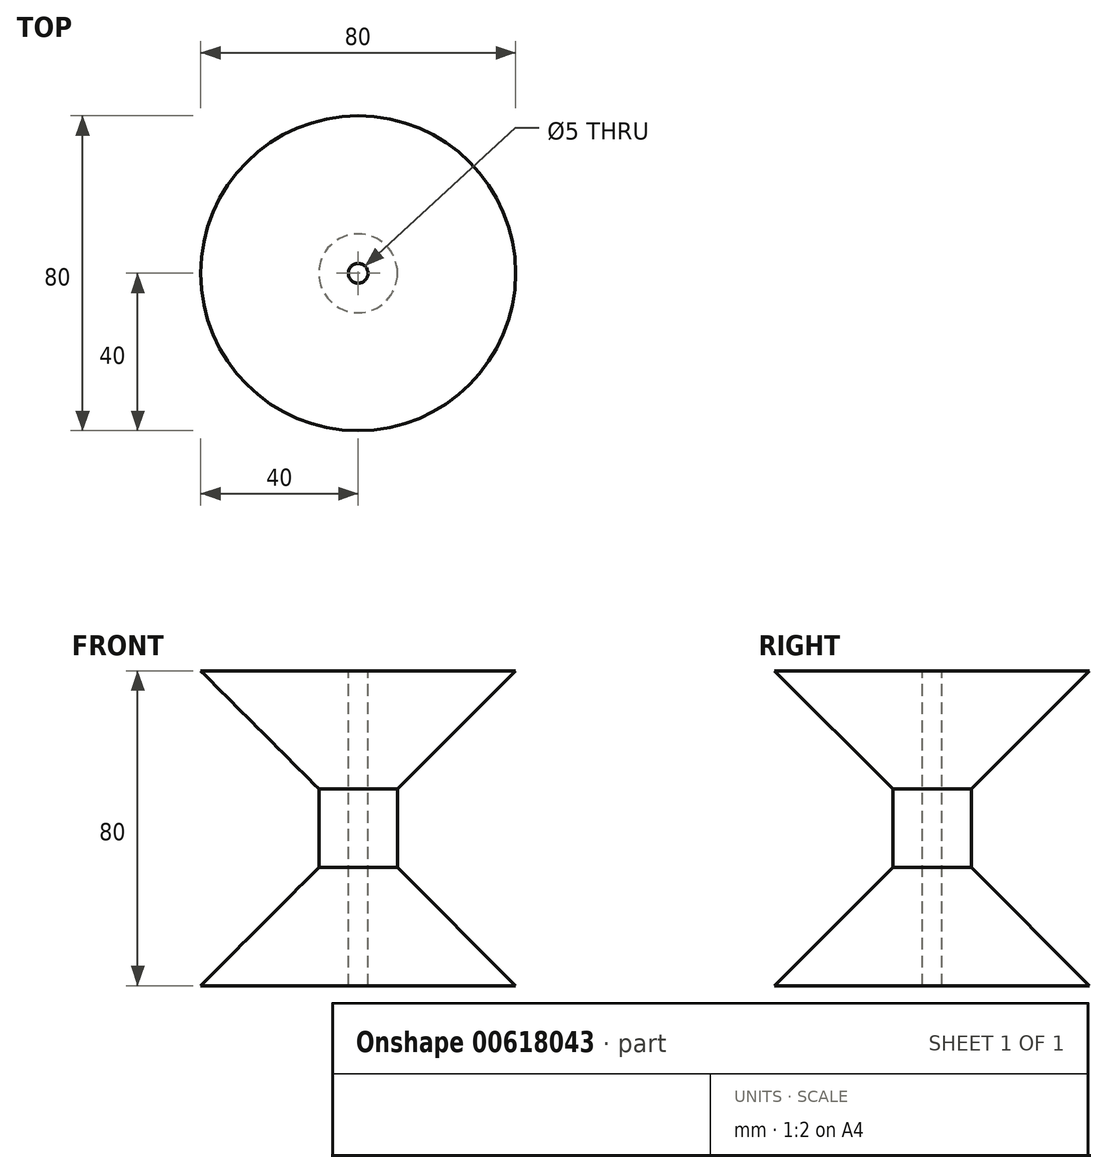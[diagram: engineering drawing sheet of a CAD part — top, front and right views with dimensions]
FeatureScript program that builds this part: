
annotation { "Feature Type Name" : "Feature", "Feature Type Description" : "" }
export const myFeature = defineFeature(function(context is Context, id is Id, definition is map)
    precondition{}
    {
        {
            var Q0;
            Q0=qCreatedBy(makeId("Front.planeOp"),FACE);
            var sketch = newSketch(context, id + "F0", { "sketchPlane" : qUnion([Q0])});
            skLineSegment(sketch, "E0", {"start": v(0, 0) * mm, "end": v(0, 80) * mm});
            skLineSegment(sketch, "E1", {"start": v(0, 80) * mm, "end": v(-40, 80) * mm});
            skLineSegment(sketch, "E2", {"start": v(-40, 80) * mm, "end": v(-10, 50) * mm});
            skLineSegment(sketch, "E3", {"start": v(-10, 50) * mm, "end": v(-10, 30) * mm});
            skLineSegment(sketch, "E4", {"start": v(-10, 30) * mm, "end": v(-40, 0) * mm});
            skLineSegment(sketch, "E5", {"start": v(-40, 0) * mm, "end": v(0, 0) * mm});
            skSolve(sketch);
        }
        {
            var Q0;
            Q0=makeQuery(id+"F0.imprint","IMPRINT",FACE,{"disambiguationData":[TD([[makeQuery(id+"F0.imprint","IMPRINT",EDGE,{"derivedFrom":sQuery(id+"F0.wireOp",EDGE,"E0")}),1.0]])]});
            var Q1;
            Q1=sQuery(id+"F0.wireOp",EDGE,"E0");
            revolve(context, id + "F1", {"entities" : qUnion([Q0]), "axis" : qUnion([Q1]), "revolveType" : RevolveType.FULL});
        }
        {
            var Q0;
            Q0=makeQuery(id+"F1.opRevolve","SWEPT_FACE",FACE,{"disambiguationData":[OSD([sQuery(id+"F0.wireOp",EDGE,"E1")])]});
            var sketch = newSketch(context, id + "F2", { "sketchPlane" : qUnion([Q0])});
            skCircle(sketch, "E6", {"center": v(0, 0) * mm, "radius": 2.5 * mm});
            skSolve(sketch);
        }
        {
            var Q0;
            Q0=makeQuery(id+"F2.imprint","IMPRINT",FACE,{"disambiguationData":[TD([[makeQuery(id+"F2.imprint","IMPRINT",EDGE,{"derivedFrom":sQuery(id+"F2.wireOp",EDGE,"E6")}),1.0]])]});
            extrude(context, id + "F3", {"entities" : qUnion([Q0]), "operationType" : NewBodyOperationType.REMOVE, "endBound" : BoundingType.UP_TO_NEXT, "oppositeDirection" : true, "depth" : 25 * mm, "offsetDistance" : 25 * mm});
        }
    });
